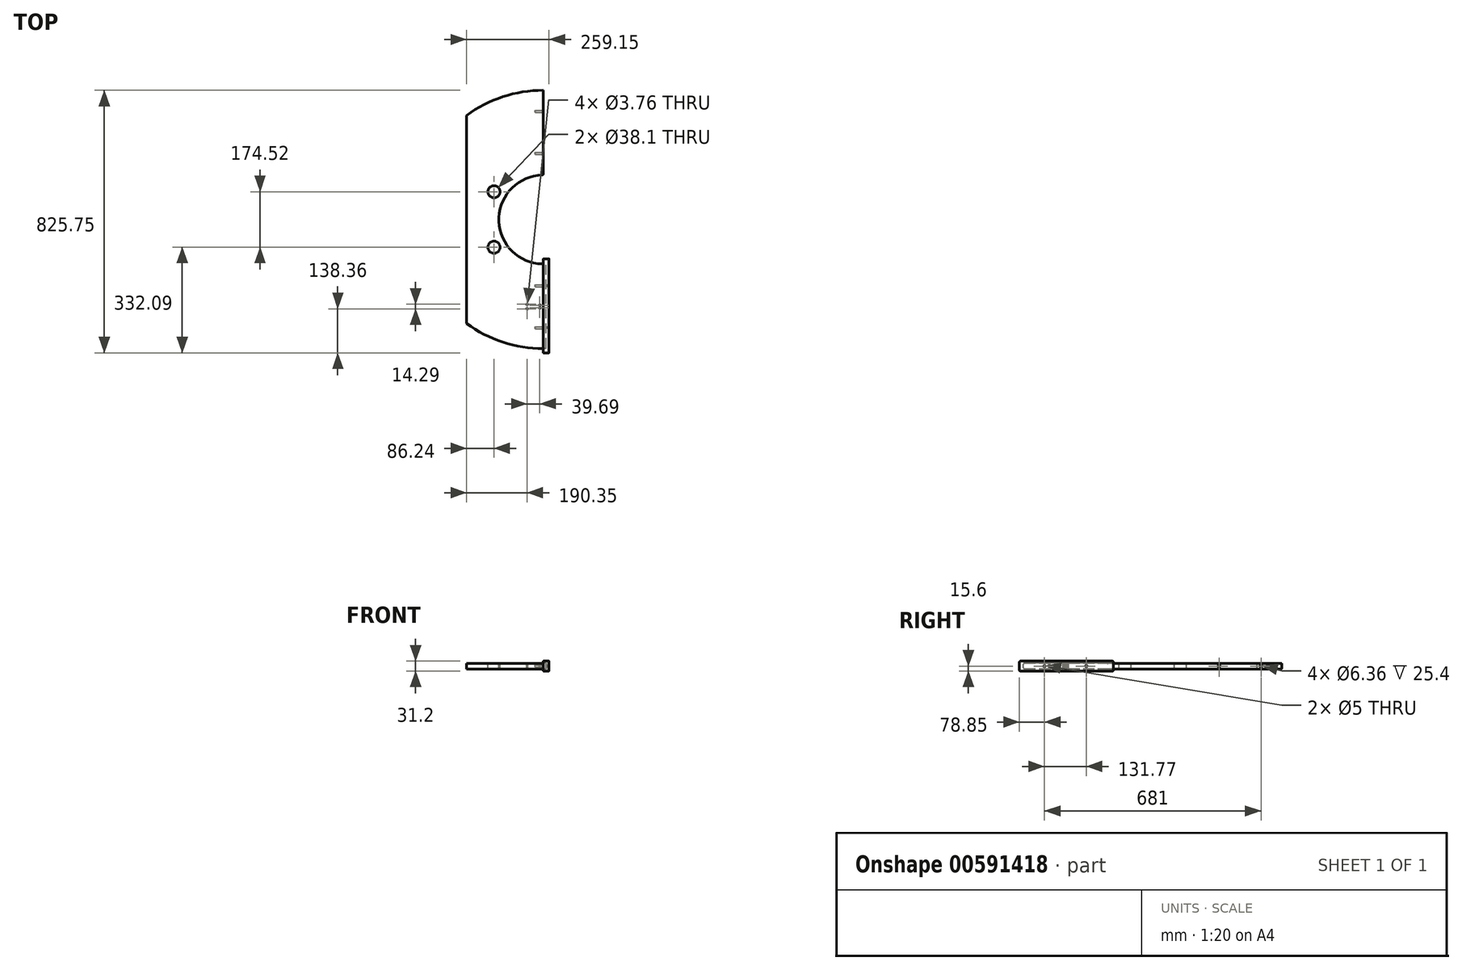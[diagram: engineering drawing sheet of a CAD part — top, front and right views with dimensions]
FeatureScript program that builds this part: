
annotation { "Feature Type Name" : "Feature", "Feature Type Description" : "" }
export const myFeature = defineFeature(function(context is Context, id is Id, definition is map)
    precondition{}
    {
        {
            var Q0;
            Q0=qCreatedBy(makeId("Top.planeOp"),FACE);
            var sketch = newSketch(context, id + "F0", { "sketchPlane" : qUnion([Q0])});
            skCircle(sketch, "E0", {"center": v(0, 0) * mm, "radius": 406.4 * mm});
            skSolve(sketch);
        }
        {
            var Q0;
            Q0 = qSketchRegion(id + "F0", true);
            extrude(context, id + "F1", {"entities" : qUnion([Q0]), "depth" : 18 * mm, "offsetDistance" : 25.4 * mm, "symmetric" : true});
        }
        {
            var Q0;
            Q0=makeQuery(id+"F1.opExtrude","CAP_FACE",FACE,{"disambiguationData":[OSD([sQuery(id+"F0.wireOp",EDGE,"E0")])],"isStart":false});
            var sketch = newSketch(context, id + "F2", { "sketchPlane" : qUnion([Q0])});
            skLineSegment(sketch, "E1.bottom", {"start": v(0, 406.4) * mm, "end": v(406.4, 406.4) * mm});
            skLineSegment(sketch, "E1.top", {"start": v(0, -406.4) * mm, "end": v(406.4, -406.4) * mm});
            skLineSegment(sketch, "E1.left", {"start": v(0, 406.4) * mm, "end": v(0, -406.4) * mm});
            skLineSegment(sketch, "E1.right", {"start": v(406.4, 406.4) * mm, "end": v(406.4, -406.4) * mm});
            skSolve(sketch);
        }
        {
            var Q0;
            Q0 = qSketchRegion(id + "F2", true);
            extrude(context, id + "F3", {"entities" : qUnion([Q0]), "operationType" : NewBodyOperationType.REMOVE, "endBound" : BoundingType.THROUGH_ALL, "oppositeDirection" : true, "depth" : 25.4 * mm, "offsetDistance" : 25.4 * mm});
        }
        {
            var Q0;
            Q0=qCreatedBy(makeId("Top.planeOp"),FACE);
            var sketch = newSketch(context, id + "F4", { "sketchPlane" : qUnion([Q0])});
            skCircle(sketch, "E2", {"center": v(0, 0) * mm, "radius": 139.7 * mm});
            skSolve(sketch);
        }
        {
            var Q0;
            Q0 = qSketchRegion(id + "F4", true);
            extrude(context, id + "F5", {"entities" : qUnion([Q0]), "operationType" : NewBodyOperationType.REMOVE, "endBound" : BoundingType.THROUGH_ALL, "depth" : 25.4 * mm, "offsetDistance" : 25.4 * mm, "hasSecondDirection" : true, "secondDirectionBound" : BoundingType.THROUGH_ALL, "secondDirectionOppositeDirection" : true, "secondDirectionDepth" : 25.4 * mm});
        }
        {
            var Q0;
            Q0=qCreatedBy(makeId("Top.planeOp"),FACE);
            var sketch = newSketch(context, id + "F6", { "sketchPlane" : qUnion([Q0])});
            skArc(sketch, "E3.0", {"start": v(0, 406.4) * mm, "mid": v(-406.4, 0) * mm, "end": v(0, -406.4) * mm, "construction": true});
            skLineSegment(sketch, "E4", {"start": v(0, 0) * mm, "end": v(-406.4, 0) * mm, "construction": true});
            skArc(sketch, "E5.0", {"start": v(0, -139.7) * mm, "mid": v(-139.7, 0) * mm, "end": v(0, 139.7) * mm, "construction": true});
            skLineSegment(sketch, "E6", {"start": v(-210.67, 6.5) * mm, "end": v(-210.67, -6.5) * mm});
            skLineSegment(sketch, "E7", {"start": v(-210.67, -6.5) * mm, "end": v(-139.55, -6.5) * mm});
            skLineSegment(sketch, "E8", {"start": v(-139.55, -6.5) * mm, "end": v(-139.55, 6.5) * mm});
            skLineSegment(sketch, "E9", {"start": v(-139.55, 6.5) * mm, "end": v(-210.67, 6.5) * mm});
            skLineSegment(sketch, "E10", {"start": v(-175.1, -6.5) * mm, "end": v(-175.1, 0) * mm, "construction": true});
            skLineSegment(sketch, "E11", {"start": v(-175.1, 0) * mm, "end": v(-175.1, 6.5) * mm, "construction": true});
            skSolve(sketch);
        }
        {
            var Q0;
            Q0 = qSketchRegion(id + "F6", true);
            extrude(context, id + "F7", {"entities" : qUnion([Q0]), "operationType" : NewBodyOperationType.REMOVE, "endBound" : BoundingType.THROUGH_ALL, "depth" : 25.4 * mm, "offsetDistance" : 25.4 * mm, "hasSecondDirection" : true, "secondDirectionBound" : BoundingType.THROUGH_ALL, "secondDirectionOppositeDirection" : true, "secondDirectionDepth" : 25.4 * mm});
        }
        {
            var Q0;
            Q0=makeQuery(id+"F7.boolean.opBoolean","COPY",EDGE,{"derivedFrom":makeQuery(id+"F7.opExtrude","SWEPT_EDGE",EDGE,{"disambiguationData":[OSD([sQuery(id+"F6.wireOp",EDGE,"E6"),sQuery(id+"F6.wireOp",EDGE,"E9")])]})});
            var Q1;
            Q1=makeQuery(id+"F7.boolean.opBoolean","COPY",EDGE,{"derivedFrom":makeQuery(id+"F7.opExtrude","SWEPT_EDGE",EDGE,{"disambiguationData":[OSD([sQuery(id+"F6.wireOp",EDGE,"E6"),sQuery(id+"F6.wireOp",EDGE,"E7")])]})});
            fillet(context, id + "F8", {"entities" : qUnion([Q0, Q1]), "radius" : 3.17 * mm, "tangentPropagation" : true, "allowEdgeOverflow" : false});
        }
        {
            var Q0;
            Q0=qCreatedBy(makeId("Front.planeOp"),FACE);
            var sketch = newSketch(context, id + "F9", { "sketchPlane" : qUnion([Q0])});
            skLineSegment(sketch, "E12", {"start": v(0, 0) * mm, "end": v(0, 127) * mm});
            skSolve(sketch);
        }
        {
            var Q0;
            Q0=makeQuery(id+"F1.opExtrude","CAP_FACE",FACE,{"disambiguationData":[OSD([sQuery(id+"F0.wireOp",EDGE,"E0")])],"isStart":false});
            var sketch = newSketch(context, id + "F10", { "sketchPlane" : qUnion([Q0])});
            skLineSegment(sketch, "E13", {"start": v(0, -266.7) * mm, "end": v(-50.8, -266.7) * mm, "construction": true});
            skLineSegment(sketch, "E14", {"start": v(-50.8, -266.7) * mm, "end": v(-50.8, -280.99) * mm, "construction": true});
            skCircle(sketch, "E15", {"center": v(-50.8, -280.99) * mm, "radius": 1.88 * mm});
            skCircle(sketch, "E16", {"center": v(-50.8, -266.7) * mm, "radius": 1.88 * mm});
            skLineSegment(sketch, "E17", {"start": v(-50.8, -273.84) * mm, "end": v(-11.11, -273.84) * mm, "construction": true});
            skLineSegment(sketch, "E18", {"start": v(-11.11, -273.84) * mm, "end": v(-11.11, -277.81) * mm, "construction": true});
            skLineSegment(sketch, "E19", {"start": v(-11.11, -273.84) * mm, "end": v(-11.11, -269.88) * mm, "construction": true});
            skCircle(sketch, "E20", {"center": v(-11.11, -277.81) * mm, "radius": 1.88 * mm});
            skCircle(sketch, "E21", {"center": v(-11.11, -269.88) * mm, "radius": 1.88 * mm});
            skSolve(sketch);
        }
        {
            var Q0;
            Q0 = qSketchRegion(id + "F10", true);
            extrude(context, id + "F11", {"entities" : qUnion([Q0]), "operationType" : NewBodyOperationType.REMOVE, "endBound" : BoundingType.THROUGH_ALL, "oppositeDirection" : true, "depth" : 25.4 * mm, "offsetDistance" : 25.4 * mm});
        }
        {
            var Q0;
            Q0 = qSketchRegion(id + "F10", true);
            extrude(context, id + "F12", {"entities" : qUnion([Q0]), "operationType" : NewBodyOperationType.REMOVE, "endBound" : BoundingType.THROUGH_ALL, "oppositeDirection" : true, "depth" : 25.4 * mm, "offsetDistance" : 25.4 * mm});
        }
        {
            var Q0;
            Q0=makeQuery(id+"F5.boolean.opBoolean","INTERSECT",EDGE,{"disambiguationData":[OD(1.0)],"derivedFrom":[makeQuery(id+"F3.boolean.opBoolean","COPY",FACE,{"derivedFrom":makeQuery(id+"F3.opExtrude","SWEPT_FACE",FACE,{"disambiguationData":[OSD([sQuery(id+"F2.wireOp",EDGE,"E1.left")])]})}),makeQuery(id+"F5.opExtrude","SWEPT_FACE",FACE,{"disambiguationData":[OSD([sQuery(id+"F4.wireOp",EDGE,"E2")])]})]});
            var Q1;
            Q1=makeQuery(id+"FZ7j7Q4fBK4hu3i_1.1.F7.boolean.opBoolean","COPY",EDGE,{"derivedFrom":makeQuery(id+"FZ7j7Q4fBK4hu3i_1.1.F7.opExtrude","SWEPT_EDGE",EDGE,{"disambiguationData":[OSD([sQuery(id+"F6.wireOp",EDGE,"E8"),sQuery(id+"F6.wireOp",EDGE,"E9")])]})});
            var Q2;
            Q2=makeQuery(id+"FZ7j7Q4fBK4hu3i_1.1.F7.boolean.opBoolean","COPY",EDGE,{"derivedFrom":makeQuery(id+"FZ7j7Q4fBK4hu3i_1.1.F7.opExtrude","SWEPT_EDGE",EDGE,{"disambiguationData":[OSD([sQuery(id+"F6.wireOp",EDGE,"E7"),sQuery(id+"F6.wireOp",EDGE,"E8")])]})});
            var Q3;
            Q3=makeQuery(id+"FZ7j7Q4fBK4hu3i_1.-1.F7.boolean.opBoolean","COPY",EDGE,{"derivedFrom":makeQuery(id+"FZ7j7Q4fBK4hu3i_1.-1.F7.opExtrude","SWEPT_EDGE",EDGE,{"disambiguationData":[OSD([sQuery(id+"F6.wireOp",EDGE,"E7"),sQuery(id+"F6.wireOp",EDGE,"E8")])]})});
            var Q4;
            Q4=makeQuery(id+"FZ7j7Q4fBK4hu3i_1.-1.F7.boolean.opBoolean","COPY",EDGE,{"derivedFrom":makeQuery(id+"FZ7j7Q4fBK4hu3i_1.-1.F7.opExtrude","SWEPT_EDGE",EDGE,{"disambiguationData":[OSD([sQuery(id+"F6.wireOp",EDGE,"E8"),sQuery(id+"F6.wireOp",EDGE,"E9")])]})});
            var Q5;
            Q5=makeQuery(id+"F5.boolean.opBoolean","INTERSECT",EDGE,{"disambiguationData":[OD(0.0)],"derivedFrom":[makeQuery(id+"F3.boolean.opBoolean","COPY",FACE,{"derivedFrom":makeQuery(id+"F3.opExtrude","SWEPT_FACE",FACE,{"disambiguationData":[OSD([sQuery(id+"F2.wireOp",EDGE,"E1.left")])]})}),makeQuery(id+"F5.opExtrude","SWEPT_FACE",FACE,{"disambiguationData":[OSD([sQuery(id+"F4.wireOp",EDGE,"E2")])]})]});
            fillet(context, id + "F13", {"entities" : qUnion([Q0, Q1, Q2, Q3, Q4, Q5]), "radius" : 3.17 * mm, "tangentPropagation" : true, "defaultsChanged" : false, "vertexSettings" : [], "allowEdgeOverflow" : false});
        }
        {
            var Q0;
            Q0=makeQuery(id+"F1.opExtrude","CAP_FACE",FACE,{"disambiguationData":[OSD([sQuery(id+"F0.wireOp",EDGE,"E0")])],"isStart":false});
            var sketch = newSketch(context, id + "F14", { "sketchPlane" : qUnion([Q0])});
            skLineSegment(sketch, "E22", {"start": v(0, 0) * mm, "end": v(-121.72, -68.56) * mm, "construction": true});
            skLineSegment(sketch, "E23", {"start": v(-121.72, -68.56) * mm, "end": v(-354.09, -199.45) * mm, "construction": true});
            skArc(sketch, "E24.0", {"start": v(-77.88, -115.98) * mm, "mid": v(-121.18, -69.51) * mm, "end": v(-139.43, -8.69) * mm, "construction": true});
            skCircle(sketch, "E25", {"center": v(-154.91, -87.26) * mm, "radius": 19.05 * mm});
            skLineSegment(sketch, "E26", {"start": v(0, 0) * mm, "end": v(-121.72, 68.56) * mm, "construction": true});
            skLineSegment(sketch, "E27", {"start": v(-121.72, 68.56) * mm, "end": v(-354.09, 199.45) * mm, "construction": true});
            skCircle(sketch, "E28", {"center": v(-154.91, 87.26) * mm, "radius": 19.05 * mm});
            skSolve(sketch);
        }
        {
            var Q0;
            Q0 = qSketchRegion(id + "F14", true);
            extrude(context, id + "F15", {"entities" : qUnion([Q0]), "operationType" : NewBodyOperationType.REMOVE, "endBound" : BoundingType.THROUGH_ALL, "oppositeDirection" : true, "depth" : 25.4 * mm, "offsetDistance" : 25.4 * mm});
        }
        {
            var Q0;
            Q0=makeQuery(id+"F1.opExtrude","CAP_FACE",FACE,{"disambiguationData":[OSD([sQuery(id+"F0.wireOp",EDGE,"E0")])],"isStart":false});
            var sketch = newSketch(context, id + "F16", { "sketchPlane" : qUnion([Q0])});
            skLineSegment(sketch, "E29.bottom", {"start": v(-406.4, 327.12) * mm, "end": v(-241.15, 327.12) * mm});
            skLineSegment(sketch, "E29.top", {"start": v(-406.4, -327.12) * mm, "end": v(-241.15, -327.12) * mm});
            skLineSegment(sketch, "E29.left", {"start": v(-406.4, 327.12) * mm, "end": v(-406.4, -327.12) * mm});
            skLineSegment(sketch, "E29.right", {"start": v(-241.15, 327.12) * mm, "end": v(-241.15, -327.12) * mm});
            skSolve(sketch);
        }
        {
            var Q0;
            Q0 = qSketchRegion(id + "F16", true);
            extrude(context, id + "F17", {"entities" : qUnion([Q0]), "operationType" : NewBodyOperationType.REMOVE, "endBound" : BoundingType.THROUGH_ALL, "oppositeDirection" : true, "depth" : 25.4 * mm, "offsetDistance" : 25.4 * mm});
        }
        {
            var Q0;
            Q0=makeQuery(id+"F17.boolean.opBoolean","COPY",EDGE,{"derivedFrom":makeQuery(id+"F17.opExtrude","SWEPT_EDGE",EDGE,{"disambiguationData":[OSD([sQuery(id+"F0.wireOp",EDGE,"E0"),sQuery(id+"F16.wireOp",EDGE,"E29.top"),sQuery(id+"F16.wireOp",EDGE,"E29.right")])]})});
            var Q1;
            Q1=makeQuery(id+"F17.boolean.opBoolean","COPY",EDGE,{"derivedFrom":makeQuery(id+"F17.opExtrude","SWEPT_EDGE",EDGE,{"disambiguationData":[OSD([sQuery(id+"F0.wireOp",EDGE,"E0"),sQuery(id+"F16.wireOp",EDGE,"E29.bottom"),sQuery(id+"F16.wireOp",EDGE,"E29.right")])]})});
            fillet(context, id + "F18", {"entities" : qUnion([Q0, Q1]), "tangentPropagation" : true, "radius" : 25.4 * mm, "defaultsChanged" : false, "vertexSettings" : [], "allowEdgeOverflow" : false});
        }
        {
            var Q0;
            Q0=makeQuery(id+"F1.opExtrude","CAP_FACE",FACE,{"disambiguationData":[OSD([sQuery(id+"F0.wireOp",EDGE,"E0")])],"isStart":false});
            var sketch = newSketch(context, id + "F19", { "sketchPlane" : qUnion([Q0])});
            skLineSegment(sketch, "E30.0", {"start": v(-139.55, -6.5) * mm, "end": v(-207.5, -6.5) * mm});
            skArc(sketch, "E30.1", {"start": v(-207.5, -6.5) * mm, "mid": v(-209.74, -5.57) * mm, "end": v(-210.67, -3.33) * mm});
            skLineSegment(sketch, "E30.2", {"start": v(-210.67, -3.33) * mm, "end": v(-210.67, 3.32) * mm});
            skArc(sketch, "E30.3", {"start": v(-210.67, 3.32) * mm, "mid": v(-209.74, 5.57) * mm, "end": v(-207.5, 6.5) * mm});
            skLineSegment(sketch, "E30.4", {"start": v(-207.5, 6.5) * mm, "end": v(-139.55, 6.5) * mm});
            skArc(sketch, "E31", {"start": v(-139.55, -6.5) * mm, "mid": v(-139.7, 0) * mm, "end": v(-139.55, 6.5) * mm});
            skSolve(sketch);
        }
        {
            var Q0;
            Q0 = qSketchRegion(id + "F19", true);
            var Q1;
            Q1=makeQuery(id+"F1.opExtrude","CAP_FACE",FACE,{"disambiguationData":[OSD([sQuery(id+"F0.wireOp",EDGE,"E0")])],"isStart":true});
            extrude(context, id + "F20", {"entities" : qUnion([Q0]), "operationType" : NewBodyOperationType.ADD, "endBound" : BoundingType.UP_TO_SURFACE, "oppositeDirection" : true, "depth" : 25.4 * mm, "endBoundEntityFace" : qUnion([Q1]), "offsetDistance" : 25.4 * mm});
        }
        {
            var Q0;
            Q0=makeQuery(id+"F5.boolean.opBoolean","SPLIT",FACE,{"disambiguationData":[OD(1.0)],"derivedFrom":makeQuery(id+"F3.boolean.opBoolean","COPY",FACE,{"derivedFrom":makeQuery(id+"F3.opExtrude","SWEPT_FACE",FACE,{"disambiguationData":[OSD([sQuery(id+"F2.wireOp",EDGE,"E1.left")])]})})});
            var sketch = newSketch(context, id + "F21", { "sketchPlane" : qUnion([Q0])});
            skLineSegment(sketch, "E32.0", {"start": v(-142.84, 9) * mm, "end": v(-406.4, 9) * mm, "construction": true});
            skLineSegment(sketch, "E32.1", {"start": v(-406.4, -9) * mm, "end": v(-406.4, 9) * mm, "construction": true});
            skLineSegment(sketch, "E32.2", {"start": v(-142.84, -9) * mm, "end": v(-142.84, 9) * mm, "construction": true});
            skLineSegment(sketch, "E33", {"start": v(-406.4, -9) * mm, "end": v(-142.84, -9) * mm, "construction": true});
            skLineSegment(sketch, "E34", {"start": v(-274.62, 9) * mm, "end": v(-274.62, -9) * mm, "construction": true});
            skLineSegment(sketch, "E35", {"start": v(-274.62, 0) * mm, "end": v(-406.4, 0) * mm, "construction": true});
            skLineSegment(sketch, "E36", {"start": v(-274.62, 0) * mm, "end": v(-142.84, 0) * mm, "construction": true});
            skCircle(sketch, "E37", {"center": v(-208.73, 0) * mm, "radius": 3.18 * mm});
            skCircle(sketch, "E38", {"center": v(-340.5, 0) * mm, "radius": 3.18 * mm});
            skCircle(sketch, "E39.MirrorC", {"center": v(208.73, 0) * mm, "radius": 3.18 * mm});
            skCircle(sketch, "E40.MirrorC", {"center": v(340.5, 0) * mm, "radius": 3.18 * mm});
            skSolve(sketch);
        }
        {
            var Q0;
            Q0 = qSketchRegion(id + "F21", true);
            extrude(context, id + "F22", {"entities" : qUnion([Q0]), "operationType" : NewBodyOperationType.REMOVE, "oppositeDirection" : true, "depth" : 25.4 * mm, "offsetDistance" : 25.4 * mm});
        }
        {
            var Q0;
            Q0=qCreatedBy(makeId("Right.planeOp"),FACE);
            var sketch = newSketch(context, id + "F23", { "sketchPlane" : qUnion([Q0])});
            skCircle(sketch, "E41.0", {"center": v(-340.5, 0) * mm, "radius": 3.17 * mm, "construction": true});
            skCircle(sketch, "E41.1", {"center": v(-208.73, 0) * mm, "radius": 3.18 * mm, "construction": true});
            skLineSegment(sketch, "E42.0", {"start": v(-406.4, -9) * mm, "end": v(-406.4, 9) * mm, "construction": true});
            skLineSegment(sketch, "E42.1", {"start": v(-142.84, 9) * mm, "end": v(-406.4, 9) * mm, "construction": true});
            skLineSegment(sketch, "E42.2", {"start": v(-393.7, -9) * mm, "end": v(-406.4, -9) * mm, "construction": true});
            skLineSegment(sketch, "E43.0", {"start": v(-142.84, -9) * mm, "end": v(-142.84, 9) * mm, "construction": true});
            skLineSegment(sketch, "E44", {"start": v(-393.7, -9) * mm, "end": v(-142.84, -9) * mm, "construction": true});
            skLineSegment(sketch, "E45.0", {"start": v(-406.65, -9.25) * mm, "end": v(-406.65, 9.25) * mm, "construction": true});
            skLineSegment(sketch, "E45.1", {"start": v(-142.59, 9.25) * mm, "end": v(-406.65, 9.25) * mm, "construction": true});
            skLineSegment(sketch, "E45.2", {"start": v(-393.7, -9.25) * mm, "end": v(-406.65, -9.25) * mm, "construction": true});
            skLineSegment(sketch, "E45.3", {"start": v(-393.7, -9.25) * mm, "end": v(-142.59, -9.25) * mm, "construction": true});
            skLineSegment(sketch, "E45.4", {"start": v(-142.59, -9.25) * mm, "end": v(-142.59, 9.25) * mm, "construction": true});
            skLineSegment(sketch, "E46", {"start": v(-142.59, -9.25) * mm, "end": v(-129.89, -9.25) * mm, "construction": true});
            skLineSegment(sketch, "E47", {"start": v(-129.89, -9.25) * mm, "end": v(-129.89, 9.25) * mm, "construction": true});
            skLineSegment(sketch, "E48", {"start": v(-129.89, 9.25) * mm, "end": v(-142.59, 9.25) * mm, "construction": true});
            skLineSegment(sketch, "E49", {"start": v(-406.65, -9.25) * mm, "end": v(-413, -9.25) * mm, "construction": true});
            skLineSegment(sketch, "E50", {"start": v(-413, -9.25) * mm, "end": v(-413, 9.25) * mm, "construction": true});
            skLineSegment(sketch, "E51", {"start": v(-413, 9.25) * mm, "end": v(-406.65, 9.25) * mm, "construction": true});
            skLineSegment(sketch, "E52.0", {"start": v(-393.7, -15.6) * mm, "end": v(-406.65, -15.6) * mm});
            skLineSegment(sketch, "E52.1", {"start": v(-393.7, -15.6) * mm, "end": v(-142.84, -15.6) * mm});
            skLineSegment(sketch, "E52.2", {"start": v(-406.65, -15.6) * mm, "end": v(-419.35, -15.6) * mm});
            skLineSegment(sketch, "E52.3", {"start": v(-142.84, -15.6) * mm, "end": v(-123.54, -15.6) * mm});
            skLineSegment(sketch, "E52.4", {"start": v(-123.54, -15.6) * mm, "end": v(-123.54, 15.6) * mm});
            skLineSegment(sketch, "E52.5", {"start": v(-419.35, -15.6) * mm, "end": v(-419.35, 15.6) * mm});
            skLineSegment(sketch, "E52.6", {"start": v(-419.35, 15.6) * mm, "end": v(-406.4, 15.6) * mm});
            skLineSegment(sketch, "E52.7", {"start": v(-142.84, 15.6) * mm, "end": v(-406.4, 15.6) * mm});
            skLineSegment(sketch, "E52.8", {"start": v(-123.54, 15.6) * mm, "end": v(-142.84, 15.6) * mm});
            skCircle(sketch, "E53", {"center": v(-340.5, 0) * mm, "radius": 2.5 * mm});
            skCircle(sketch, "E54", {"center": v(-208.73, 0) * mm, "radius": 2.5 * mm});
            skSolve(sketch);
        }
        {
            var Q0;
            Q0 = qSketchRegion(id + "F23", true);
            extrude(context, id + "F24", {"entities" : qUnion([Q0]), "depth" : 18 * mm, "offsetDistance" : 25.4 * mm});
        }
        {
            var Q0;
            Q0=makeQuery(id+"F23.imprint","IMPRINT",FACE,{"disambiguationData":[TD([[makeQuery(id+"F23.imprint","IMPRINT",EDGE,{"derivedFrom":sQuery(id+"F23.wireOp",EDGE,"E52.0")}),-1.0]])]});
            var sketch = newSketch(context, id + "F25", { "sketchPlane" : qUnion([Q0])});
            skLineSegment(sketch, "E55.0", {"start": v(-142.59, 9.25) * mm, "end": v(-406.4, 9.25) * mm});
            skLineSegment(sketch, "E55.4", {"start": v(-393.7, -9.25) * mm, "end": v(-406.4, -9.25) * mm});
            skLineSegment(sketch, "E55.5", {"start": v(-393.7, -9.25) * mm, "end": v(-142.59, -9.25) * mm});
            skLineSegment(sketch, "E55.6", {"start": v(-129.89, 9.25) * mm, "end": v(-142.59, 9.25) * mm});
            skLineSegment(sketch, "E55.7", {"start": v(-129.89, -9.25) * mm, "end": v(-129.89, 9.25) * mm});
            skLineSegment(sketch, "E55.8", {"start": v(-142.59, -9.25) * mm, "end": v(-129.89, -9.25) * mm});
            skLineSegment(sketch, "E56.0", {"start": v(-406.4, -9) * mm, "end": v(-406.4, 9) * mm});
            skLineSegment(sketch, "E57", {"start": v(-406.4, -9) * mm, "end": v(-406.4, -9.25) * mm});
            skLineSegment(sketch, "E58", {"start": v(-406.4, 9) * mm, "end": v(-406.4, 9.25) * mm});
            skPoint(sketch, "E59.orphan", {"position": v(-406.65, 9.25) * mm});
            skPoint(sketch, "E60.orphan", {"position": v(-406.65, -9.25) * mm});
            skSolve(sketch);
        }
        {
            var Q0;
            Q0 = qSketchRegion(id + "F25", true);
            extrude(context, id + "F26", {"entities" : qUnion([Q0]), "operationType" : NewBodyOperationType.REMOVE, "depth" : 9 * mm, "offsetDistance" : 25.4 * mm});
        }
        {
            var Q0;
            Q0=makeQuery(id+"F24.opExtrude","CAP_FACE",FACE,{"disambiguationData":[OSD([sQuery(id+"F23.wireOp",EDGE,"E52.0"),sQuery(id+"F23.wireOp",EDGE,"E52.1"),sQuery(id+"F23.wireOp",EDGE,"E52.2"),sQuery(id+"F23.wireOp",EDGE,"E52.3"),sQuery(id+"F23.wireOp",EDGE,"E52.4"),sQuery(id+"F23.wireOp",EDGE,"E52.5"),sQuery(id+"F23.wireOp",EDGE,"E52.6"),sQuery(id+"F23.wireOp",EDGE,"E52.7"),sQuery(id+"F23.wireOp",EDGE,"E52.8"),sQuery(id+"F23.wireOp",EDGE,"E53"),sQuery(id+"F23.wireOp",EDGE,"E54")])],"isStart":true});
            var sketch = newSketch(context, id + "F27", { "sketchPlane" : qUnion([Q0])});
            skLineSegment(sketch, "E61.0", {"start": v(129.89, -9.25) * mm, "end": v(129.89, 9.25) * mm});
            skLineSegment(sketch, "E62", {"start": v(129.89, 9.25) * mm, "end": v(123.54, 9.25) * mm});
            skLineSegment(sketch, "E63", {"start": v(123.54, 9.25) * mm, "end": v(123.54, -9.25) * mm});
            skLineSegment(sketch, "E64", {"start": v(123.54, -9.25) * mm, "end": v(129.89, -9.25) * mm});
            skSolve(sketch);
        }
        {
            var Q0;
            Q0 = qSketchRegion(id + "F27", true);
            var Q1;
            Q1=makeQuery(id+"F26.boolean.opBoolean","COPY",FACE,{"derivedFrom":makeQuery(id+"F26.opExtrude","CAP_FACE",FACE,{"disambiguationData":[OSD([sQuery(id+"F25.wireOp",EDGE,"E55.0"),sQuery(id+"F25.wireOp",EDGE,"E55.1"),sQuery(id+"F25.wireOp",EDGE,"E55.2"),sQuery(id+"F25.wireOp",EDGE,"E55.3"),sQuery(id+"F25.wireOp",EDGE,"E55.4"),sQuery(id+"F25.wireOp",EDGE,"E55.5"),sQuery(id+"F25.wireOp",EDGE,"E55.6"),sQuery(id+"F25.wireOp",EDGE,"E55.7"),sQuery(id+"F25.wireOp",EDGE,"E55.8")])],"isStart":false})});
            extrude(context, id + "F28", {"entities" : qUnion([Q0]), "operationType" : NewBodyOperationType.REMOVE, "endBound" : BoundingType.UP_TO_SURFACE, "oppositeDirection" : true, "depth" : 25.4 * mm, "endBoundEntityFace" : qUnion([Q1]), "offsetDistance" : 25.4 * mm});
        }
        {
            var Q0;
            Q0=makeQuery(id+"F1.opExtrude","CAP_EDGE",EDGE,{"disambiguationData":[OSD([sQuery(id+"F0.wireOp",EDGE,"E0")])],"isStart":false});
            var Q1;
            Q1=makeQuery(id+"F1.opExtrude","CAP_EDGE",EDGE,{"disambiguationData":[OSD([sQuery(id+"F0.wireOp",EDGE,"E0")])],"isStart":true});
            fillet(context, id + "F29", {"entities" : qUnion([Q0, Q1]), "radius" : 3.17 * mm, "tangentPropagation" : true, "allowEdgeOverflow" : false});
        }
        {
            var Q0;
            Q0=makeQuery(id+"F26.boolean.opBoolean","COPY",EDGE,{"derivedFrom":makeQuery(id+"F26.opExtrude","SWEPT_EDGE",EDGE,{"disambiguationData":[OSD([sQuery(id+"F25.wireOp",EDGE,"E55.0"),sQuery(id+"F25.wireOp",EDGE,"E58")])]})});
            var Q1;
            Q1=makeQuery(id+"F26.boolean.opBoolean","COPY",EDGE,{"derivedFrom":makeQuery(id+"F26.opExtrude","SWEPT_EDGE",EDGE,{"disambiguationData":[OSD([sQuery(id+"F25.wireOp",EDGE,"E55.4"),sQuery(id+"F25.wireOp",EDGE,"E57")])]})});
            fillet(context, id + "F30", {"entities" : qUnion([Q0, Q1]), "radius" : 3.17 * mm, "tangentPropagation" : true, "allowEdgeOverflow" : false});
        }
        {
            var Q0;
            Q0=makeQuery(id+"F24.opExtrude","SWEPT_EDGE",EDGE,{"disambiguationData":[OSD([sQuery(id+"F23.wireOp",EDGE,"E52.5"),sQuery(id+"F23.wireOp",EDGE,"E52.6")])]});
            var Q1;
            Q1=makeQuery(id+"F24.opExtrude","SWEPT_EDGE",EDGE,{"disambiguationData":[OSD([sQuery(id+"F23.wireOp",EDGE,"E52.2"),sQuery(id+"F23.wireOp",EDGE,"E52.5")])]});
            var Q2;
            Q2=makeQuery(id+"F24.opExtrude","SWEPT_EDGE",EDGE,{"disambiguationData":[OSD([sQuery(id+"F23.wireOp",EDGE,"E52.4"),sQuery(id+"F23.wireOp",EDGE,"E52.8")])]});
            var Q3;
            Q3=makeQuery(id+"F24.opExtrude","SWEPT_EDGE",EDGE,{"disambiguationData":[OSD([sQuery(id+"F23.wireOp",EDGE,"E52.3"),sQuery(id+"F23.wireOp",EDGE,"E52.4")])]});
            fillet(context, id + "F31", {"entities" : qUnion([Q0, Q1, Q2, Q3]), "radius" : 3.17 * mm, "tangentPropagation" : true, "allowEdgeOverflow" : false});
        }
    });
